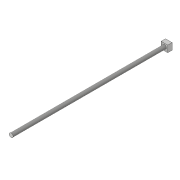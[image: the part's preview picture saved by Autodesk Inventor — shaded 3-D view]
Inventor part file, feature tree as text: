
AUTODESK INVENTOR PART (.ipt)
format: ipt  version: 2019 (Build 230136000, 136)  size: 92,672 bytes
history: native  units: in
note: dims shown in document units (in); Inventor stores cm internally (conversion verified against a paired STEP export)
features: extrude x3, sketch x3, thread x2, plane x1
ambient origin geometry x8: Origin, YZ Plane, XZ Plane, XY Plane, X Axis, Y Axis, Z Axis, Center Point
bodies: Solid1 (feature_tree)
feature tree (9):
  extrude  "Extrusion1"  Depth=0.5906in
  extrude  "Extrusion2"  Depth=0.3937in TaperAngle=0.0deg
  thread  "Thread1"  [1 undecoded]
  plane  "Work Plane1"
  extrude  "Extrusion3"  Depth=0.3937in
  thread  "Thread2"  [1 undecoded]
  sketch  "Sketch1"  dims[d0=0.5906in d1=0.5906in]
  sketch  "Sketch2"  dims[d2=0.3937in d3=0.0in d5=9.8425in d6=0.0in d7=0.3937in d8=0.0in]
  sketch  "Sketch3"  dims[d9=0.0in d10=0.3543in d11=3.937in d12=0.0in d13=0.3937in d14=0.0in d15=0.3543in]
note: 2 required parameter values undecoded (feature->parameter linkage not recoverable at this tier; creation-order binding heuristic only, values carry confidence <= 0.55)
